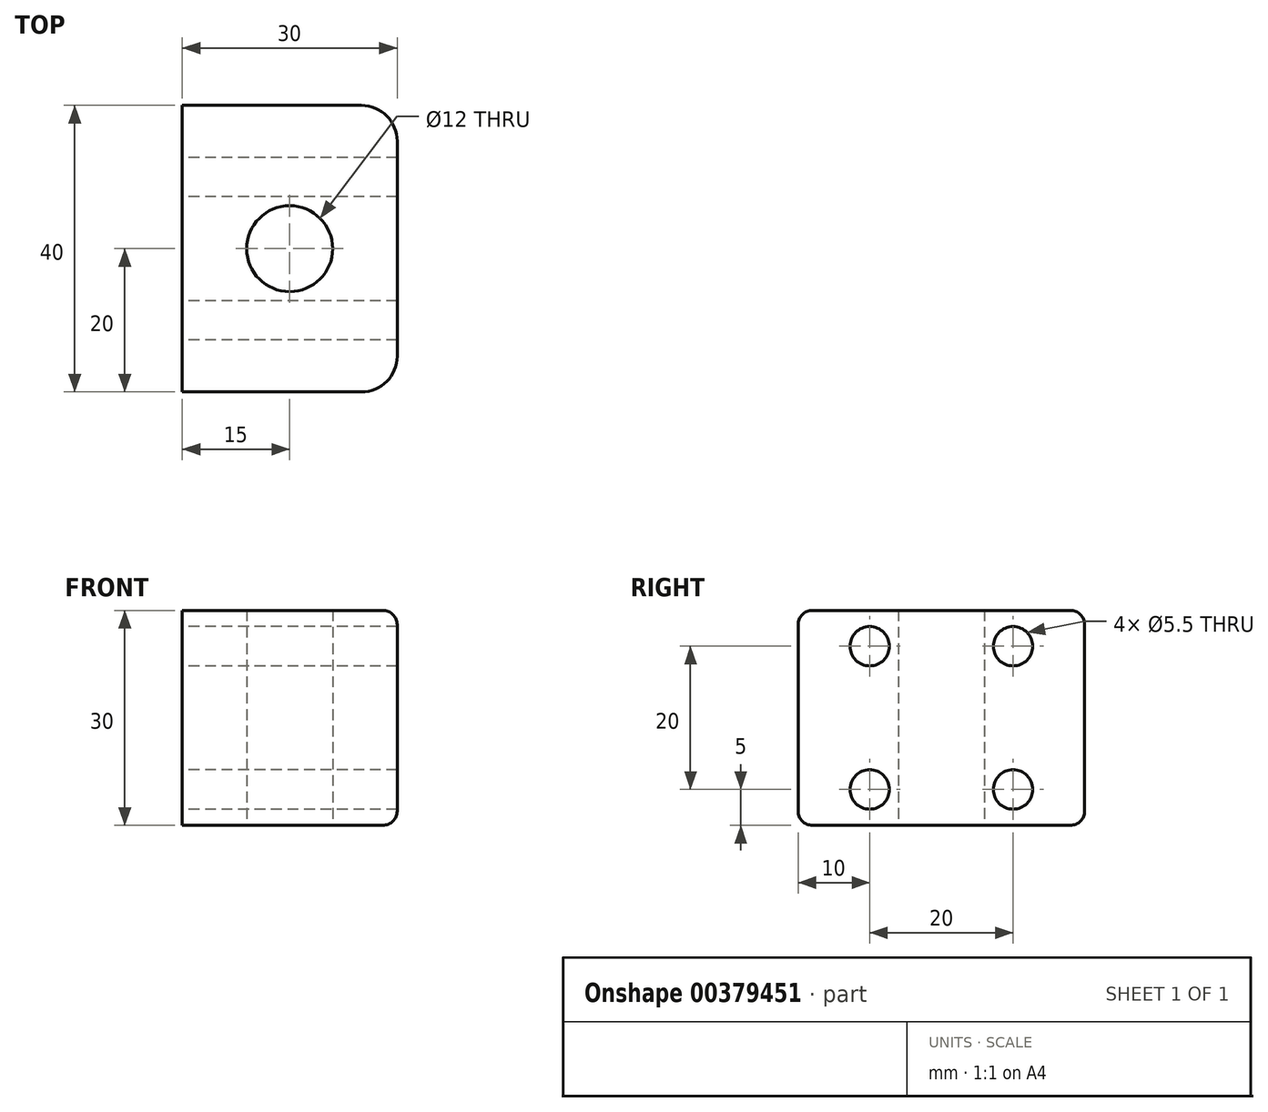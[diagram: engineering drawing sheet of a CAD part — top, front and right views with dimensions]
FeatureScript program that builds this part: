
annotation { "Feature Type Name" : "Feature", "Feature Type Description" : "" }
export const myFeature = defineFeature(function(context is Context, id is Id, definition is map)
    precondition{}
    {
        {
            var Q0;
            Q0=qCreatedBy(makeId("Front.planeOp"),FACE);
            var sketch = newSketch(context, id + "F0", { "sketchPlane" : qUnion([Q0])});
            skLineSegment(sketch, "E0.bottom", {"start": v(0, 0) * mm, "end": v(30, 0) * mm});
            skLineSegment(sketch, "E0.top", {"start": v(0, 30) * mm, "end": v(30, 30) * mm});
            skLineSegment(sketch, "E0.left", {"start": v(0, 0) * mm, "end": v(0, 30) * mm});
            skLineSegment(sketch, "E0.right", {"start": v(30, 0) * mm, "end": v(30, 30) * mm});
            skSolve(sketch);
        }
        {
            var Q0;
            Q0=makeQuery(id+"F0.imprint","IMPRINT",FACE,{"disambiguationData":[TD([[makeQuery(id+"F0.imprint","IMPRINT",EDGE,{"derivedFrom":sQuery(id+"F0.wireOp",EDGE,"E0.bottom")}),1.0]])]});
            extrude(context, id + "F1", {"entities" : qUnion([Q0]), "depth" : 40 * mm});
        }
        {
            var Q0;
            Q0=makeQuery(id+"F1.opExtrude","SWEPT_FACE",FACE,{"disambiguationData":[OSD([sQuery(id+"F0.wireOp",EDGE,"E0.top")])]});
            var sketch = newSketch(context, id + "F2", { "sketchPlane" : qUnion([Q0])});
            skLineSegment(sketch, "E1", {"start": v(0, 0) * mm, "end": v(30, -40) * mm});
            skLineSegment(sketch, "E2", {"start": v(30, 0) * mm, "end": v(0, -40) * mm});
            skPoint(sketch, "E3", {"position": v(15, -20) * mm});
            skSolve(sketch);
        }
        {
            var Q0;
            Q0=sQuery(id+"F2.wireOp",VERTEX,"E3");
            var Q1;
            Q1=makeQuery(id+"F1.opExtrude","SWEPT_BODY",BODY,{"disambiguationData":[OSD([sQuery(id+"F0.wireOp",EDGE,"E0.bottom"),sQuery(id+"F0.wireOp",EDGE,"E0.top"),sQuery(id+"F0.wireOp",EDGE,"E0.left"),sQuery(id+"F0.wireOp",EDGE,"E0.right")])]});
            hole(context, id + "F3", {"style" : HoleStyle.SIMPLE, "endStyle" : HoleEndStyle.THROUGH, "holeDiameter" : 12 * mm, "isTappedThrough" : true, "tappedDepth" : 12 * mm, "tapClearance" : 3, "locations" : qUnion([Q0]), "scope" : qUnion([Q1])});
        }
        {
            var Q0;
            Q0=makeQuery(id+"F1.opExtrude","SWEPT_FACE",FACE,{"disambiguationData":[OSD([sQuery(id+"F0.wireOp",EDGE,"E0.right")])]});
            var sketch = newSketch(context, id + "F4", { "sketchPlane" : qUnion([Q0])});
            skLineSegment(sketch, "E4", {"start": v(-40, 30) * mm, "end": v(-40, 0) * mm});
            skLineSegment(sketch, "E5", {"start": v(-10, 30) * mm, "end": v(-10, 25) * mm});
            skLineSegment(sketch, "E6", {"start": v(-10, 0) * mm, "end": v(-10, 5) * mm});
            skLineSegment(sketch, "E7", {"start": v(-30, 0) * mm, "end": v(-30, 5) * mm});
            skLineSegment(sketch, "E8", {"start": v(-30, 30) * mm, "end": v(-30, 25) * mm});
            skPoint(sketch, "E9", {"position": v(-30, 25) * mm});
            skPoint(sketch, "E10", {"position": v(-30, 5) * mm});
            skPoint(sketch, "E11", {"position": v(-10, 5) * mm});
            skPoint(sketch, "E12", {"position": v(-10, 25) * mm});
            skSolve(sketch);
        }
        {
            var Q0;
            Q0=sQuery(id+"F4.wireOp",VERTEX,"E9");
            var Q1;
            Q1=sQuery(id+"F4.wireOp",VERTEX,"E12");
            var Q2;
            Q2=sQuery(id+"F4.wireOp",VERTEX,"E11");
            var Q3;
            Q3=sQuery(id+"F4.wireOp",VERTEX,"E10");
            var Q4;
            Q4=makeQuery(id+"F1.opExtrude","SWEPT_BODY",BODY,{"disambiguationData":[OSD([sQuery(id+"F0.wireOp",EDGE,"E0.bottom"),sQuery(id+"F0.wireOp",EDGE,"E0.top"),sQuery(id+"F0.wireOp",EDGE,"E0.left"),sQuery(id+"F0.wireOp",EDGE,"E0.right")])]});
            hole(context, id + "F5", {"style" : HoleStyle.SIMPLE, "endStyle" : HoleEndStyle.THROUGH, "standardTappedOrClearance" : lookupTablePath({ "standard" : "ISO", "fit" : "Normal", "size" : "M5", "type" : "Clearance" }), "standardBlindInLast" : lookupTablePath({ "fit" : "Standard", "standard" : "ISO", "size" : "M5", "type" : "Clearance" }), "holeDiameter" : 5.5 * mm, "isTappedThrough" : true, "tappedDepth" : 12 * mm, "tapClearance" : 3, "locations" : qUnion([Q0, Q1, Q2, Q3]), "scope" : qUnion([Q4])});
        }
        {
            var Q0;
            Q0=makeQuery(id+"F1.opExtrude","CAP_EDGE",EDGE,{"disambiguationData":[OSD([sQuery(id+"F0.wireOp",EDGE,"E0.right")])],"isStart":true});
            var Q1;
            Q1=makeQuery(id+"F1.opExtrude","CAP_EDGE",EDGE,{"disambiguationData":[OSD([sQuery(id+"F0.wireOp",EDGE,"E0.right")])],"isStart":false});
            fillet(context, id + "F6", {"entities" : qUnion([Q0, Q1]), "radius" : 5 * mm, "tangentPropagation" : true, "allowEdgeOverflow" : false});
        }
        {
            var Q0;
            Q0=makeQuery(id+"F1.opExtrude","SWEPT_EDGE",EDGE,{"disambiguationData":[OSD([sQuery(id+"F0.wireOp",EDGE,"E0.top"),sQuery(id+"F0.wireOp",EDGE,"E0.right")])]});
            var Q1;
            Q1=makeQuery(id+"F1.opExtrude","SWEPT_EDGE",EDGE,{"disambiguationData":[OSD([sQuery(id+"F0.wireOp",EDGE,"E0.bottom"),sQuery(id+"F0.wireOp",EDGE,"E0.right")])]});
            fillet(context, id + "F7", {"entities" : qUnion([Q0, Q1]), "radius" : 2 * mm, "tangentPropagation" : true, "allowEdgeOverflow" : false});
        }
    });
